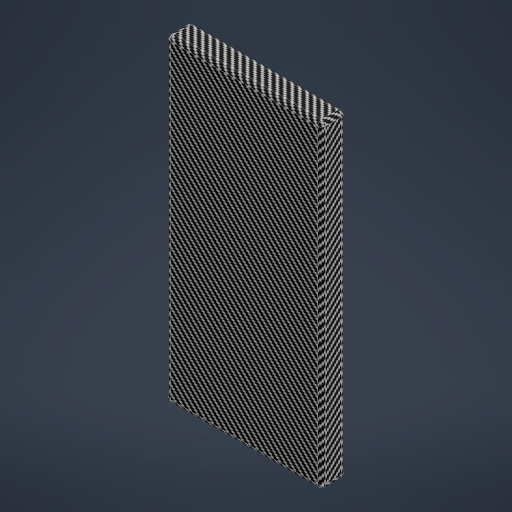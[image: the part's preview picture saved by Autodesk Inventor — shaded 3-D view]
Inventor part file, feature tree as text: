
AUTODESK INVENTOR PART (.ipt)
format: ipt  version: 2023.2 (Build 272271000, 271)  size: 327,680 bytes
history: native  units: mm
features: sketch x1
ambient origin geometry x8: Origin, YZ Plane, XZ Plane, XY Plane, X Axis, Y Axis, Z Axis, Center Point
bodies: Body1 (feature_tree)
feature tree (1):
  sketch  "Sketch1"  dims[d228=78.0mm d229=160.0mm d230=12.0mm d231=0.0mm d232=2.0mm d9=0.5mm d10=0.872665mm d11=0.5mm d12=0.872665mm d13=0.5mm d14=0.872665mm d27=0.5mm d28=0.872665mm d29=0.5mm d30=0.872665mm d88=0.5mm d89=0.872665mm d90=0.5mm d91=0.872665mm d116=0.5mm d117=0.872665mm d118=0.5mm d119=0.872665mm d154=0.5mm d155=0.872665mm d156=0.5mm d157=0.872665mm d181=0.5mm d182=0.872665mm d183=0.5mm d184=0.872665mm d221=0.5mm d222=0.872665mm d223=0.5mm d224=0.872665mm]
